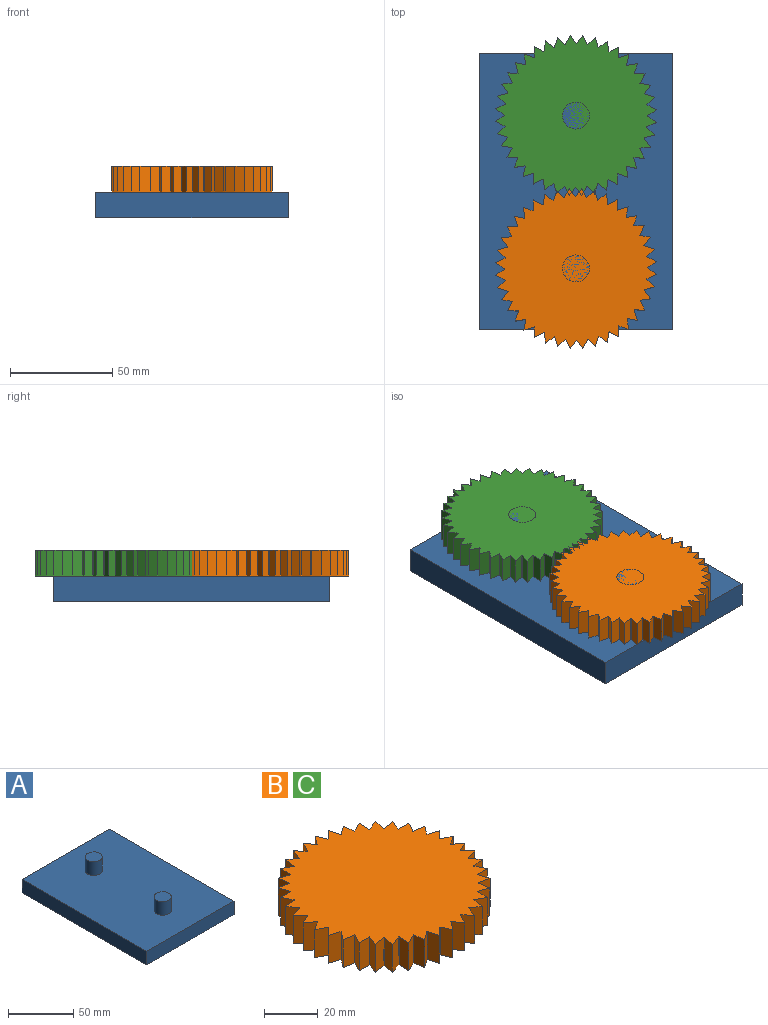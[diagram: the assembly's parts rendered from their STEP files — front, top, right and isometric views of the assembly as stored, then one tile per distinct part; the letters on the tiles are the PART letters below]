
ASSEMBLY  parts=3 mates=2
PART A: 10 faces, bbox 94.4x135.4x25.4 mm
  f0: plane 94.39x12.7mm, normal (0,1,0), area 1198.8mm2, adj f1,f3,f4,f5
  f1: plane 135.36x12.7mm, normal (-1,0,0), area 1719mm2, adj f0,f2,f4,f5
  f2: plane 94.39x12.7mm, normal (0,-1,0), area 1198.8mm2, adj f1,f3,f4,f5
  f3: plane 135.36x12.7mm, normal (1,0,0), area 1719mm2, adj f0,f2,f4,f5
  f4: plane 135.36x94.39mm, normal (0,0,1), area 12503.8mm2, adj f0,f1,f2,f3,f6,f8
  f5: plane 135.36x94.39mm, normal (0,0,-1), area 12776.4mm2, adj f0,f1,f2,f3
  f6: cylinder r=6.59mm len=13.17mm, axis (0,0,-1), area 525.6mm2, adj f4,f7
  f7: plane 13.17x13.17mm, normal (0,0,1), area 136.3mm2, adj f6
  f8: cylinder r=6.59mm len=13.17mm, axis (0,0,-1), area 525.6mm2, adj f4,f9
  f9: plane 13.17x13.17mm, normal (0,0,1), area 136.3mm2, adj f8
PART B: 122 faces, bbox 78.7x78.7x12.7 mm
  f0: plane 12.7x4.66mm, normal (0.46,0.89,0), area 66.8mm2, adj f1,f119,f120,f121
  f1: cylinder r=35.1mm len=12.7mm, axis (0,0,-1), area 2.4mm2, adj f0,f2,f120,f121
  f2: plane 12.7x3.73mm, normal (0.68,-0.73,0), area 65mm2, adj f1,f3,f120,f121
  f3: plane 12.7x4.99mm, normal (0.32,0.95,0), area 66.8mm2, adj f2,f4,f120,f121
  f4: cylinder r=35.1mm len=12.7mm, axis (0,0,-1), area 2.4mm2, adj f3,f5,f120,f121
  f5: plane 12.7x4.04mm, normal (0.79,-0.61,0), area 65mm2, adj f4,f6,f120,f121
  f6: plane 12.7x5.19mm, normal (0.17,0.99,0), area 66.8mm2, adj f5,f7,f120,f121
  f7: cylinder r=35.1mm len=12.7mm, axis (0,0,-1), area 2.4mm2, adj f6,f8,f120,f121
  f8: plane 12.7x4.48mm, normal (0.88,-0.48,0), area 65mm2, adj f7,f9,f120,f121
  f9: plane 12.7x5.26mm, normal (0.01,1,0), area 66.8mm2, adj f8,f10,f120,f121
  f10: cylinder r=35.1mm len=12.7mm, axis (0,0,-1), area 2.4mm2, adj f9,f11,f120,f121
  f11: plane 12.7x4.81mm, normal (0.94,-0.34,0), area 65mm2, adj f10,f12,f120,f121
  f12: plane 12.7x5.2mm, normal (-0.15,0.99,0), area 66.8mm2, adj f11,f13,f120,f121
  f13: cylinder r=35.1mm len=12.7mm, axis (0,0,-1), area 2.4mm2, adj f12,f14,f120,f121
  f14: plane 12.7x5.03mm, normal (0.98,-0.19,0), area 65mm2, adj f13,f15,f120,f121
  f15: plane 12.7x5.02mm, normal (-0.3,0.95,0), area 66.8mm2, adj f14,f16,f120,f121
  f16: cylinder r=35.1mm len=12.7mm, axis (0,0,-1), area 2.4mm2, adj f15,f17,f120,f121
  f17: plane 12.7x5.11mm, normal (1,-0.03,0), area 65mm2, adj f16,f18,f120,f121
  f18: plane 12.7x4.71mm, normal (-0.45,0.9,0), area 66.8mm2, adj f17,f19,f120,f121
  f19: cylinder r=35.1mm len=12.7mm, axis (0,0,-1), area 2.4mm2, adj f18,f20,f120,f121
  f20: plane 12.7x5.08mm, normal (0.99,0.12,0), area 65mm2, adj f19,f21,f120,f121
  f21: plane 12.7x4.28mm, normal (-0.58,0.81,0), area 66.8mm2, adj f20,f22,f120,f121
  f22: cylinder r=35.1mm len=12.7mm, axis (0,0,-1), area 2.4mm2, adj f21,f23,f120,f121
  f23: plane 12.7x4.91mm, normal (0.96,0.28,0), area 65mm2, adj f22,f24,f120,f121
  f24: plane 12.7x3.75mm, normal (-0.7,0.71,0), area 66.8mm2, adj f23,f25,f120,f121
  f25: cylinder r=35.1mm len=12.7mm, axis (0,0,-1), area 2.4mm2, adj f24,f26,f120,f121
  f26: plane 12.7x4.63mm, normal (0.9,0.43,0), area 65mm2, adj f25,f27,f120,f121
  f27: plane 12.7x4.23mm, normal (-0.8,0.6,0), area 66.8mm2, adj f26,f28,f120,f121
  f28: cylinder r=35.1mm len=12.7mm, axis (0,0,-1), area 2.4mm2, adj f27,f29,f120,f121
  f29: plane 12.7x4.23mm, normal (0.83,0.56,0), area 65mm2, adj f28,f30,f120,f121
  f30: plane 12.7x4.66mm, normal (-0.89,0.46,0), area 66.8mm2, adj f29,f31,f120,f121
  f31: cylinder r=35.1mm len=12.7mm, axis (0,0,-1), area 2.4mm2, adj f30,f32,f120,f121
  f32: plane 12.7x3.73mm, normal (0.73,0.68,0), area 65mm2, adj f31,f33,f120,f121
  f33: plane 12.7x4.99mm, normal (-0.95,0.32,0), area 66.8mm2, adj f32,f34,f120,f121
  f34: cylinder r=35.1mm len=12.7mm, axis (0,0,-1), area 2.4mm2, adj f33,f35,f120,f121
  f35: plane 12.7x4.04mm, normal (0.61,0.79,0), area 65mm2, adj f34,f36,f120,f121
  f36: plane 12.7x5.19mm, normal (-0.99,0.17,0), area 66.8mm2, adj f35,f37,f120,f121
  f37: cylinder r=35.1mm len=12.7mm, axis (0,0,-1), area 2.4mm2, adj f36,f38,f120,f121
  f38: plane 12.7x4.48mm, normal (0.48,0.88,0), area 65mm2, adj f37,f39,f120,f121
  f39: plane 12.7x5.26mm, normal (-1,0.01,0), area 66.8mm2, adj f38,f40,f120,f121
  f40: cylinder r=35.1mm len=12.7mm, axis (0,0,-1), area 2.4mm2, adj f39,f41,f120,f121
  f41: plane 12.7x4.81mm, normal (0.34,0.94,0), area 65mm2, adj f40,f42,f120,f121
  f42: plane 12.7x5.2mm, normal (-0.99,-0.15,0), area 66.8mm2, adj f41,f43,f120,f121
  f43: cylinder r=35.1mm len=12.7mm, axis (0,0,-1), area 2.4mm2, adj f42,f44,f120,f121
  f44: plane 12.7x5.03mm, normal (0.19,0.98,0), area 65mm2, adj f43,f45,f120,f121
  f45: plane 12.7x5.02mm, normal (-0.95,-0.3,0), area 66.8mm2, adj f44,f46,f120,f121
  f46: cylinder r=35.1mm len=12.7mm, axis (0,0,-1), area 2.4mm2, adj f45,f47,f120,f121
  f47: plane 12.7x5.11mm, normal (0.03,1,0), area 65mm2, adj f46,f48,f120,f121
  f48: plane 12.7x4.71mm, normal (-0.9,-0.45,0), area 66.8mm2, adj f47,f49,f120,f121
  f49: cylinder r=35.1mm len=12.7mm, axis (0,0,-1), area 2.4mm2, adj f48,f50,f120,f121
  f50: plane 12.7x5.08mm, normal (-0.12,0.99,0), area 65mm2, adj f49,f51,f120,f121
  f51: plane 12.7x4.28mm, normal (-0.81,-0.58,0), area 66.8mm2, adj f50,f52,f120,f121
  f52: cylinder r=35.1mm len=12.7mm, axis (0,0,-1), area 2.4mm2, adj f51,f53,f120,f121
  f53: plane 12.7x4.91mm, normal (-0.28,0.96,0), area 65mm2, adj f52,f54,f120,f121
  f54: plane 12.7x3.75mm, normal (-0.71,-0.7,0), area 66.8mm2, adj f53,f55,f120,f121
  f55: cylinder r=35.1mm len=12.7mm, axis (0,0,-1), area 2.4mm2, adj f54,f56,f120,f121
  f56: plane 12.7x4.63mm, normal (-0.43,0.9,0), area 65mm2, adj f55,f57,f120,f121
  f57: plane 12.7x4.23mm, normal (-0.6,-0.8,0), area 66.8mm2, adj f56,f58,f120,f121
  f58: cylinder r=35.1mm len=12.7mm, axis (0,0,-1), area 2.4mm2, adj f57,f59,f120,f121
  f59: plane 12.7x4.23mm, normal (-0.56,0.83,0), area 65mm2, adj f58,f60,f120,f121
  f60: plane 12.7x4.66mm, normal (-0.46,-0.89,0), area 66.8mm2, adj f59,f61,f120,f121
  f61: cylinder r=35.1mm len=12.7mm, axis (0,0,-1), area 2.4mm2, adj f60,f62,f120,f121
  f62: plane 12.7x3.73mm, normal (-0.68,0.73,0), area 65mm2, adj f61,f63,f120,f121
  f63: plane 12.7x4.99mm, normal (-0.32,-0.95,0), area 66.8mm2, adj f62,f64,f120,f121
  f64: cylinder r=35.1mm len=12.7mm, axis (0,0,-1), area 2.4mm2, adj f63,f65,f120,f121
  f65: plane 12.7x4.04mm, normal (-0.79,0.61,0), area 65mm2, adj f64,f66,f120,f121
  f66: plane 12.7x5.19mm, normal (-0.17,-0.99,0), area 66.8mm2, adj f65,f67,f120,f121
  f67: cylinder r=35.1mm len=12.7mm, axis (0,0,-1), area 2.4mm2, adj f66,f68,f120,f121
  f68: plane 12.7x4.48mm, normal (-0.88,0.48,0), area 65mm2, adj f67,f69,f120,f121
  f69: plane 12.7x5.26mm, normal (-0.01,-1,0), area 66.8mm2, adj f68,f70,f120,f121
  f70: cylinder r=35.1mm len=12.7mm, axis (0,0,-1), area 2.4mm2, adj f69,f71,f120,f121
  f71: plane 12.7x4.81mm, normal (-0.94,0.34,0), area 65mm2, adj f70,f72,f120,f121
  f72: plane 12.7x5.2mm, normal (0.15,-0.99,0), area 66.8mm2, adj f71,f73,f120,f121
  f73: cylinder r=35.1mm len=12.7mm, axis (0,0,-1), area 2.4mm2, adj f72,f74,f120,f121
  f74: plane 12.7x5.03mm, normal (-0.98,0.19,0), area 65mm2, adj f73,f75,f120,f121
  f75: plane 12.7x5.02mm, normal (0.3,-0.95,0), area 66.8mm2, adj f74,f76,f120,f121
  f76: cylinder r=35.1mm len=12.7mm, axis (0,0,-1), area 2.4mm2, adj f75,f77,f120,f121
  f77: plane 12.7x5.11mm, normal (-1,0.03,0), area 65mm2, adj f76,f78,f120,f121
  f78: plane 12.7x4.71mm, normal (0.45,-0.9,0), area 66.8mm2, adj f77,f79,f120,f121
  f79: cylinder r=35.1mm len=12.7mm, axis (0,0,-1), area 2.4mm2, adj f78,f80,f120,f121
  f80: plane 12.7x5.08mm, normal (-0.99,-0.12,0), area 65mm2, adj f79,f81,f120,f121
  f81: plane 12.7x4.28mm, normal (0.58,-0.81,0), area 66.8mm2, adj f80,f82,f120,f121
  f82: cylinder r=35.1mm len=12.7mm, axis (0,0,-1), area 2.4mm2, adj f81,f83,f120,f121
  f83: plane 12.7x4.91mm, normal (-0.96,-0.28,0), area 65mm2, adj f82,f84,f120,f121
  f84: plane 12.7x3.75mm, normal (0.7,-0.71,0), area 66.8mm2, adj f83,f85,f120,f121
  f85: cylinder r=35.1mm len=12.7mm, axis (0,0,-1), area 2.4mm2, adj f84,f86,f120,f121
  f86: plane 12.7x4.63mm, normal (-0.9,-0.43,0), area 65mm2, adj f85,f87,f120,f121
  f87: plane 12.7x4.23mm, normal (0.8,-0.6,0), area 66.8mm2, adj f86,f88,f120,f121
  f88: cylinder r=35.1mm len=12.7mm, axis (0,0,-1), area 2.4mm2, adj f87,f89,f120,f121
  f89: plane 12.7x4.23mm, normal (-0.83,-0.56,0), area 65mm2, adj f88,f90,f120,f121
  f90: plane 12.7x4.66mm, normal (0.89,-0.46,0), area 66.8mm2, adj f89,f91,f120,f121
  f91: cylinder r=35.1mm len=12.7mm, axis (0,0,-1), area 2.4mm2, adj f90,f92,f120,f121
  f92: plane 12.7x3.73mm, normal (-0.73,-0.68,0), area 65mm2, adj f91,f93,f120,f121
  f93: plane 12.7x4.99mm, normal (0.95,-0.32,0), area 66.8mm2, adj f92,f94,f120,f121
  f94: cylinder r=35.1mm len=12.7mm, axis (0,0,-1), area 2.4mm2, adj f93,f95,f120,f121
  f95: plane 12.7x4.04mm, normal (-0.61,-0.79,0), area 65mm2, adj f94,f96,f120,f121
  f96: plane 12.7x5.19mm, normal (0.99,-0.17,0), area 66.8mm2, adj f95,f97,f120,f121
  f97: cylinder r=35.1mm len=12.7mm, axis (0,0,-1), area 2.4mm2, adj f96,f98,f120,f121
  f98: plane 12.7x4.48mm, normal (-0.48,-0.88,0), area 65mm2, adj f97,f99,f120,f121
  f99: plane 12.7x5.26mm, normal (1,-0.01,0), area 66.8mm2, adj f98,f100,f120,f121
  f100: cylinder r=35.1mm len=12.7mm, axis (0,0,-1), area 2.4mm2, adj f99,f101,f120,f121
  f101: plane 12.7x4.81mm, normal (-0.34,-0.94,0), area 65mm2, adj f100,f102,f120,f121
  f102: plane 12.7x5.2mm, normal (0.99,0.15,0), area 66.8mm2, adj f101,f103,f120,f121
  f103: cylinder r=35.1mm len=12.7mm, axis (0,0,-1), area 2.4mm2, adj f102,f104,f120,f121
  f104: plane 12.7x5.03mm, normal (-0.19,-0.98,0), area 65mm2, adj f103,f105,f120,f121
  f105: plane 12.7x5.02mm, normal (0.95,0.3,0), area 66.8mm2, adj f104,f106,f120,f121
  f106: cylinder r=35.1mm len=12.7mm, axis (0,0,-1), area 2.4mm2, adj f105,f107,f120,f121
  f107: plane 12.7x5.11mm, normal (-0.03,-1,0), area 65mm2, adj f106,f108,f120,f121
  f108: plane 12.7x4.71mm, normal (0.9,0.45,0), area 66.8mm2, adj f107,f109,f120,f121
  f109: cylinder r=35.1mm len=12.7mm, axis (0,0,-1), area 2.4mm2, adj f108,f110,f120,f121
  f110: plane 12.7x5.08mm, normal (0.12,-0.99,0), area 65mm2, adj f109,f111,f120,f121
  f111: plane 12.7x4.28mm, normal (0.81,0.58,0), area 66.8mm2, adj f110,f112,f120,f121
  f112: cylinder r=35.1mm len=12.7mm, axis (0,0,-1), area 2.4mm2, adj f111,f113,f120,f121
  f113: plane 12.7x4.91mm, normal (0.28,-0.96,0), area 65mm2, adj f112,f114,f120,f121
  f114: plane 12.7x3.75mm, normal (0.71,0.7,0), area 66.8mm2, adj f113,f115,f120,f121
  f115: cylinder r=35.1mm len=12.7mm, axis (0,0,-1), area 2.4mm2, adj f114,f116,f120,f121
  f116: plane 12.7x4.63mm, normal (0.43,-0.9,0), area 65mm2, adj f115,f117,f120,f121
  f117: plane 12.7x4.23mm, normal (0.6,0.8,0), area 66.8mm2, adj f116,f118,f120,f121
  f118: cylinder r=35.1mm len=12.7mm, axis (0,0,-1), area 2.4mm2, adj f117,f119,f120,f121
  f119: plane 12.7x4.23mm, normal (0.56,-0.83,0), area 65mm2, adj f0,f118,f120,f121
  f120: plane 78.66x78.66mm, normal (0,0,1), area 4329.5mm2, adj f0,f1,f2,f3,f4,f5,f6,f7
  f121: plane 78.66x78.66mm, normal (0,0,-1), area 4329.5mm2, adj f0,f1,f2,f3,f4,f5,f6,f7
PART C: same geometry as B
PLACE A t=(19.82,18.35,-20.7)mm fixed
PLACE B rot(axis=(0,0,-1),107.6deg) t=(19.82,-36.7,-8)mm
PLACE C rot(axis=(0,0,1),107.6deg) t=(19.82,38.1,-8)mm
MATE revolute B.f1 <-> A.f6  axis (0,0,-1) through (19.82,-36.7,-8)mm
MATE revolute C.f1 <-> A.f8  axis (0,0,-1) through (19.82,38.1,-8)mm
